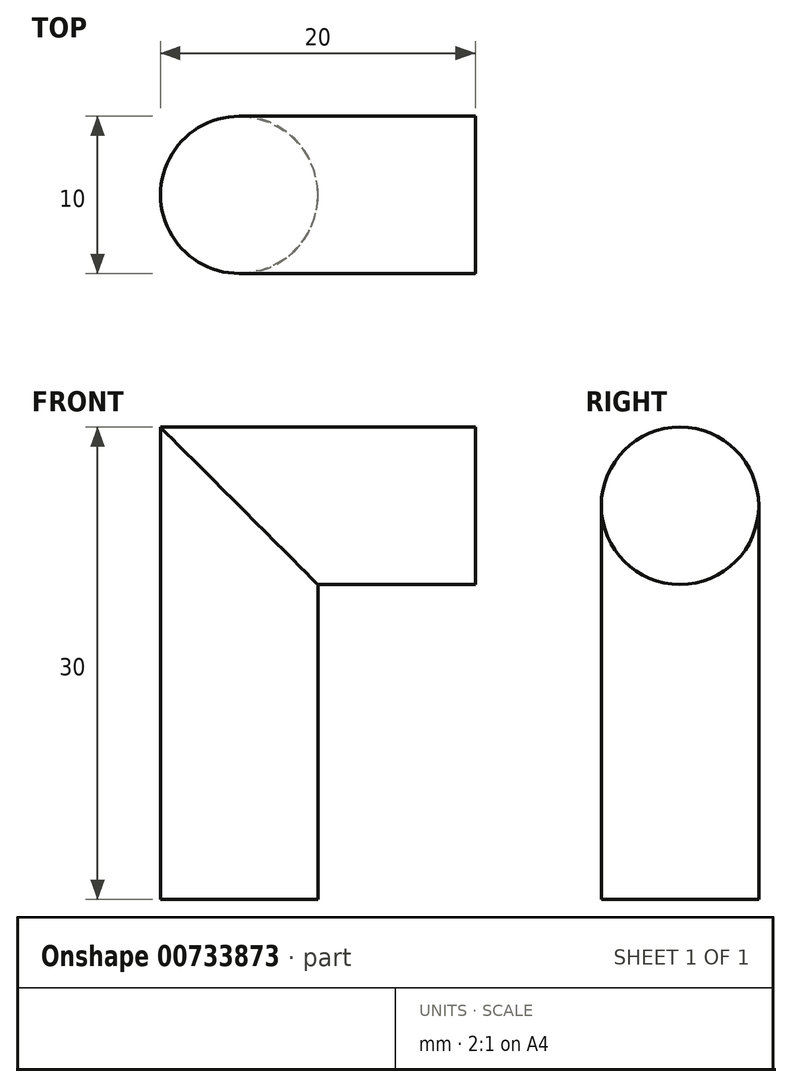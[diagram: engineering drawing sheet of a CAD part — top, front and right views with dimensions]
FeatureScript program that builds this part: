
annotation { "Feature Type Name" : "Feature", "Feature Type Description" : "" }
export const myFeature = defineFeature(function(context is Context, id is Id, definition is map)
    precondition{}
    {
        {
            var Q0;
            Q0=qCreatedBy(makeId("Front.planeOp"),FACE);
            var sketch = newSketch(context, id + "F0", { "sketchPlane" : qUnion([Q0])});
            skLineSegment(sketch, "E0", {"start": v(0, 0) * mm, "end": v(0, 30) * mm});
            skLineSegment(sketch, "E1", {"start": v(0, 30) * mm, "end": v(20, 30) * mm});
            skLineSegment(sketch, "E2.0", {"start": v(10, 20) * mm, "end": v(20, 20) * mm});
            skLineSegment(sketch, "E2.1", {"start": v(10, 0) * mm, "end": v(10, 20) * mm});
            skLineSegment(sketch, "E3", {"start": v(20, 20) * mm, "end": v(20, 30) * mm});
            skLineSegment(sketch, "E4", {"start": v(0, 0) * mm, "end": v(10, 0) * mm});
            skSolve(sketch);
        }
        {
            var Q0;
            Q0=makeQuery(id+"F0.imprint","IMPRINT",FACE,{"disambiguationData":[TD([[makeQuery(id+"F0.imprint","IMPRINT",EDGE,{"derivedFrom":sQuery(id+"F0.wireOp",EDGE,"E0")}),-1.0]])]});
            extrude(context, id + "F1", {"entities" : qUnion([Q0]), "depth" : 10 * mm, "offsetDistance" : 25 * mm});
        }
        {
            var Q0;
            Q0=makeQuery(id+"F1.opExtrude","CAP_EDGE",EDGE,{"disambiguationData":[OSD([sQuery(id+"F0.wireOp",EDGE,"E1")])],"isStart":false});
            var Q1;
            Q1=makeQuery(id+"F1.opExtrude","CAP_EDGE",EDGE,{"disambiguationData":[OSD([sQuery(id+"F0.wireOp",EDGE,"E1")])],"isStart":true});
            var Q2;
            Q2=makeQuery(id+"F1.opExtrude","CAP_EDGE",EDGE,{"disambiguationData":[OSD([sQuery(id+"F0.wireOp",EDGE,"E0")])],"isStart":false});
            var Q3;
            Q3=makeQuery(id+"F1.opExtrude","CAP_EDGE",EDGE,{"disambiguationData":[OSD([sQuery(id+"F0.wireOp",EDGE,"E2.1")])],"isStart":false});
            var Q4;
            Q4=makeQuery(id+"F1.opExtrude","CAP_EDGE",EDGE,{"disambiguationData":[OSD([sQuery(id+"F0.wireOp",EDGE,"E2.0")])],"isStart":false});
            var Q5;
            Q5=makeQuery(id+"F1.opExtrude","CAP_EDGE",EDGE,{"disambiguationData":[OSD([sQuery(id+"F0.wireOp",EDGE,"E2.1")])],"isStart":true});
            var Q6;
            Q6=makeQuery(id+"F1.opExtrude","CAP_EDGE",EDGE,{"disambiguationData":[OSD([sQuery(id+"F0.wireOp",EDGE,"E2.0")])],"isStart":true});
            var Q7;
            Q7=makeQuery(id+"F1.opExtrude","CAP_EDGE",EDGE,{"disambiguationData":[OSD([sQuery(id+"F0.wireOp",EDGE,"E0")])],"isStart":true});
            fillet(context, id + "F2", {"entities" : qUnion([Q0, Q1, Q2, Q3, Q4, Q5, Q6, Q7]), "radius" : 5 * mm, "tangentPropagation" : true, "allowEdgeOverflow" : false});
        }
    });
